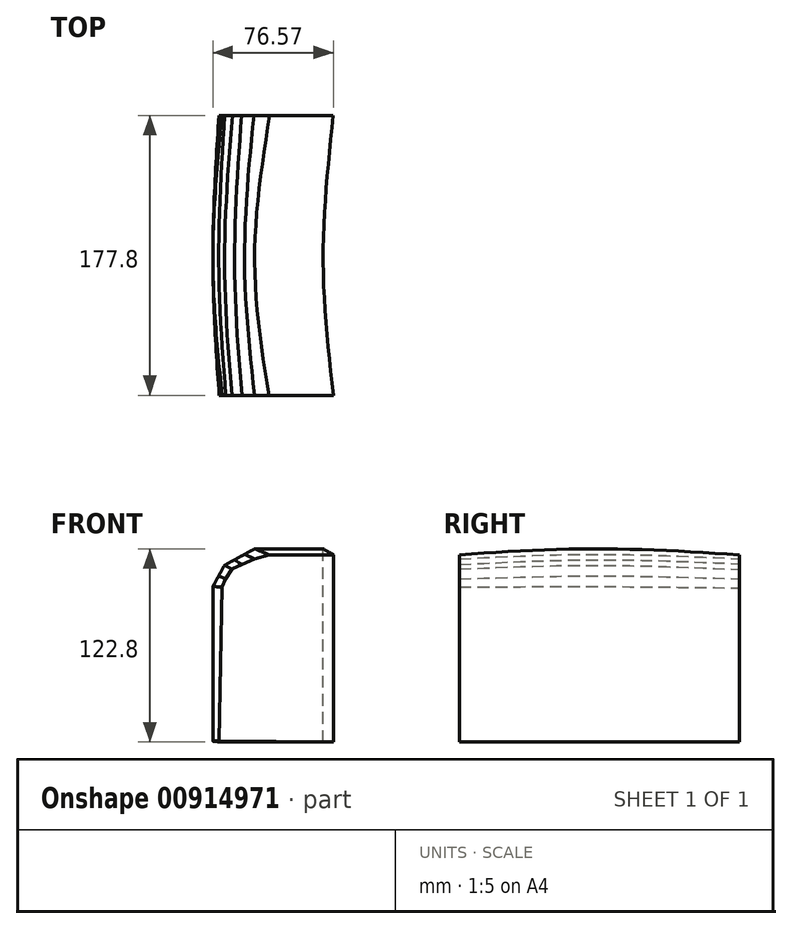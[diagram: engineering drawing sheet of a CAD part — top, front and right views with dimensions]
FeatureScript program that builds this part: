
annotation { "Feature Type Name" : "Feature", "Feature Type Description" : "" }
export const myFeature = defineFeature(function(context is Context, id is Id, definition is map)
    precondition{}
    {
        {
            var Q0;
            Q0=qCreatedBy(makeId("Front.planeOp"),FACE);
            var sketch = newSketch(context, id + "F0", { "sketchPlane" : qUnion([Q0])});
            skLineSegment(sketch, "E0", {"start": v(-40.98, -56.39) * mm, "end": v(-39.16, 41.24) * mm});
            skLineSegment(sketch, "E1", {"start": v(-39.16, 41.24) * mm, "end": v(-37.33, 46.99) * mm});
            skLineSegment(sketch, "E2", {"start": v(-37.33, 46.99) * mm, "end": v(-32.37, 53) * mm});
            skLineSegment(sketch, "E3", {"start": v(-32.37, 53) * mm, "end": v(-26.63, 56.65) * mm});
            skLineSegment(sketch, "E4", {"start": v(-26.63, 56.65) * mm, "end": v(-18.8, 59.78) * mm});
            skLineSegment(sketch, "E5", {"start": v(-18.8, 59.78) * mm, "end": v(-8.88, 62.39) * mm});
            skLineSegment(sketch, "E6", {"start": v(-8.88, 62.39) * mm, "end": v(31.59, 62.39) * mm});
            skLineSegment(sketch, "E7", {"start": v(31.59, 62.39) * mm, "end": v(31.59, -56.39) * mm});
            skLineSegment(sketch, "E8", {"start": v(31.59, -56.39) * mm, "end": v(-40.98, -56.39) * mm});
            skSolve(sketch);
        }
        {
            var Q0;
            Q0=qCreatedBy(makeId("Front.planeOp"),FACE);
            cPlane(context, id + "F1", {"entities" : qUnion([Q0]), "cplaneType" : CPlaneType.OFFSET, "offset" : 177.8 * mm, "width" : 152.4 * mm, "height" : 152.4 * mm});
        }
        {
            var Q0;
            Q0=qCreatedBy(id+"F1.planeOp",FACE);
            var sketch = newSketch(context, id + "F2", { "sketchPlane" : qUnion([Q0])});
            skLineSegment(sketch, "E9", {"start": v(-40.84, -55.86) * mm, "end": v(-39, 41.77) * mm});
            skLineSegment(sketch, "E10", {"start": v(-39, 41.77) * mm, "end": v(-36.66, 46.99) * mm});
            skLineSegment(sketch, "E11", {"start": v(-36.66, 46.99) * mm, "end": v(-32.74, 53.25) * mm});
            skLineSegment(sketch, "E12", {"start": v(-32.74, 53.25) * mm, "end": v(-26.48, 56.12) * mm});
            skLineSegment(sketch, "E13", {"start": v(-26.48, 56.12) * mm, "end": v(-18.39, 59.78) * mm});
            skLineSegment(sketch, "E14", {"start": v(-18.39, 59.78) * mm, "end": v(-9.25, 62.39) * mm});
            skLineSegment(sketch, "E15", {"start": v(-9.25, 62.39) * mm, "end": v(31.73, 62.39) * mm});
            skLineSegment(sketch, "E16", {"start": v(31.73, 62.39) * mm, "end": v(31.73, -56.65) * mm});
            skLineSegment(sketch, "E17", {"start": v(31.73, -56.65) * mm, "end": v(-40.84, -55.86) * mm});
            skSolve(sketch);
        }
        {
            var Q0;
            Q0=qCreatedBy(makeId("Front.planeOp"),FACE);
            cPlane(context, id + "F3", {"entities" : qUnion([Q0]), "cplaneType" : CPlaneType.OFFSET, "offset" : 96.27 * mm, "width" : 152.4 * mm, "height" : 152.4 * mm});
        }
        {
            var Q0;
            Q0=qCreatedBy(id+"F3.planeOp",FACE);
            var sketch = newSketch(context, id + "F4", { "sketchPlane" : qUnion([Q0])});
            skLineSegment(sketch, "E18", {"start": v(-44.81, -56.12) * mm, "end": v(-44.81, 42.2) * mm});
            skLineSegment(sketch, "E19", {"start": v(-44.81, 42.2) * mm, "end": v(-37.42, 55.69) * mm});
            skLineSegment(sketch, "E20", {"start": v(-37.42, 55.69) * mm, "end": v(-18.27, 66.13) * mm});
            skLineSegment(sketch, "E21", {"start": v(-18.27, 66.13) * mm, "end": v(25.23, 66.13) * mm});
            skLineSegment(sketch, "E22", {"start": v(25.23, 66.13) * mm, "end": v(25.23, -56.56) * mm});
            skLineSegment(sketch, "E23", {"start": v(25.23, -56.56) * mm, "end": v(-44.81, -56.12) * mm});
            skSolve(sketch);
        }
        {
            var Q0;
            Q0=makeQuery(id+"F2.imprint","IMPRINT",FACE,{"disambiguationData":[TD([[makeQuery(id+"F2.imprint","IMPRINT",EDGE,{"derivedFrom":sQuery(id+"F2.wireOp",EDGE,"E9")}),-1.0]])]});
            var Q1;
            Q1=makeQuery(id+"F4.imprint","IMPRINT",FACE,{"disambiguationData":[TD([[makeQuery(id+"F4.imprint","IMPRINT",EDGE,{"derivedFrom":sQuery(id+"F4.wireOp",EDGE,"E18")}),-1.0]])]});
            var Q2;
            Q2=makeQuery(id+"F0.imprint","IMPRINT",FACE,{"disambiguationData":[TD([[makeQuery(id+"F0.imprint","IMPRINT",EDGE,{"derivedFrom":sQuery(id+"F0.wireOp",EDGE,"E0")}),-1.0]])]});
            loft(context, id + "F5", {"sheetProfilesArray" : [{ "sheetProfileEntities" : qUnion([Q0]) }, { "sheetProfileEntities" : qUnion([Q1]) }, { "sheetProfileEntities" : qUnion([Q2]) }]});
        }
    });
